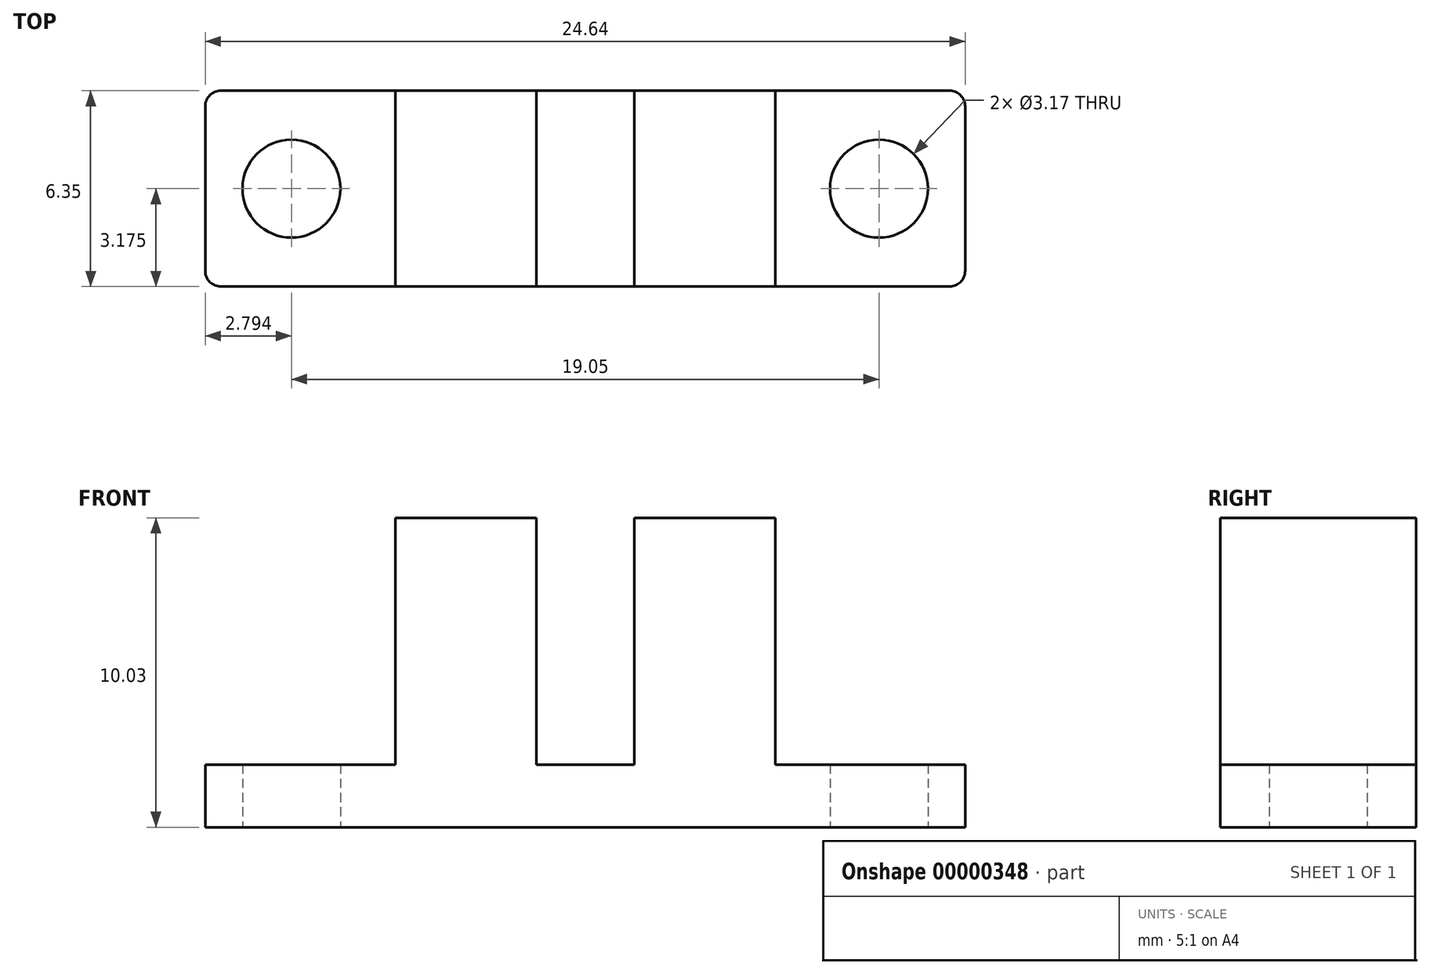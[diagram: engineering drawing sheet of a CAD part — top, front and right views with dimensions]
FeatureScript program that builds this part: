
annotation { "Feature Type Name" : "Feature", "Feature Type Description" : "" }
export const myFeature = defineFeature(function(context is Context, id is Id, definition is map)
    precondition{}
    {
        {
            var Q0;
            Q0=qCreatedBy(makeId("Top.planeOp"),FACE);
            var sketch = newSketch(context, id + "F0", { "sketchPlane" : qUnion([Q0])});
            skLineSegment(sketch, "E0.bottom", {"start": v(0.5, 0) * mm, "end": v(24.13, 0) * mm});
            skLineSegment(sketch, "E0.top", {"start": v(0.5, 6.35) * mm, "end": v(24.13, 6.35) * mm});
            skLineSegment(sketch, "E0.left", {"start": v(0, 0.5) * mm, "end": v(0, 5.84) * mm});
            skLineSegment(sketch, "E0.right", {"start": v(24.64, 0.5) * mm, "end": v(24.64, 5.84) * mm});
            skPoint(sketch, "E1.visualSharp", {"position": v(0, 6.35) * mm});
            skArc(sketch, "E1.filletArc", {"start": v(0.5, 6.35) * mm, "mid": v(0.15, 6.2) * mm, "end": v(0, 5.84) * mm});
            skPoint(sketch, "E2.visualSharp", {"position": v(0, 0) * mm});
            skArc(sketch, "E2.filletArc", {"start": v(0, 0.5) * mm, "mid": v(0.15, 0.15) * mm, "end": v(0.5, 0) * mm});
            skPoint(sketch, "E3.visualSharp", {"position": v(24.64, 0) * mm});
            skArc(sketch, "E3.filletArc", {"start": v(24.13, 0) * mm, "mid": v(24.49, 0.15) * mm, "end": v(24.64, 0.5) * mm});
            skPoint(sketch, "E4.visualSharp", {"position": v(24.64, 6.35) * mm});
            skArc(sketch, "E4.filletArc", {"start": v(24.64, 5.84) * mm, "mid": v(24.49, 6.2) * mm, "end": v(24.13, 6.35) * mm});
            skCircle(sketch, "E5", {"center": v(2.8, 3.18) * mm, "radius": 1.59 * mm});
            skCircle(sketch, "E6", {"center": v(21.84, 3.18) * mm, "radius": 1.59 * mm});
            skSolve(sketch);
        }
        {
            var Q0;
            Q0 = qSketchRegion(id + "F0", true);
            extrude(context, id + "F1", {"entities" : qUnion([Q0]), "depth" : 2.03 * mm});
        }
        {
            var Q0;
            Q0=makeQuery(id+"F1.opExtrude","CAP_FACE",FACE,{"disambiguationData":[OSD([sQuery(id+"F0.wireOp",EDGE,"E0.bottom"),sQuery(id+"F0.wireOp",EDGE,"E0.top"),sQuery(id+"F0.wireOp",EDGE,"E0.left"),sQuery(id+"F0.wireOp",EDGE,"E0.right"),sQuery(id+"F0.wireOp",EDGE,"E1.filletArc"),sQuery(id+"F0.wireOp",EDGE,"E2.filletArc"),sQuery(id+"F0.wireOp",EDGE,"E3.filletArc"),sQuery(id+"F0.wireOp",EDGE,"E4.filletArc"),sQuery(id+"F0.wireOp",EDGE,"E5"),sQuery(id+"F0.wireOp",EDGE,"E6")])],"isStart":false});
            var sketch = newSketch(context, id + "F2", { "sketchPlane" : qUnion([Q0])});
            skLineSegment(sketch, "E7.bottom", {"start": v(6.16, 6.35) * mm, "end": v(10.73, 6.35) * mm});
            skLineSegment(sketch, "E7.top", {"start": v(6.16, 0) * mm, "end": v(10.73, 0) * mm});
            skLineSegment(sketch, "E7.left", {"start": v(6.16, 6.35) * mm, "end": v(6.16, 0) * mm});
            skLineSegment(sketch, "E7.right", {"start": v(10.73, 6.35) * mm, "end": v(10.73, 0) * mm});
            skLineSegment(sketch, "E8.bottom", {"start": v(13.9, 6.35) * mm, "end": v(18.48, 6.35) * mm});
            skLineSegment(sketch, "E8.top", {"start": v(13.9, 0) * mm, "end": v(18.48, 0) * mm});
            skLineSegment(sketch, "E8.left", {"start": v(13.9, 6.35) * mm, "end": v(13.9, 0) * mm});
            skLineSegment(sketch, "E8.right", {"start": v(18.48, 6.35) * mm, "end": v(18.48, 0) * mm});
            skSolve(sketch);
        }
        {
            var Q0;
            Q0 = qSketchRegion(id + "F2", true);
            extrude(context, id + "F3", {"entities" : qUnion([Q0]), "operationType" : NewBodyOperationType.ADD, "depth" : 8 * mm});
        }
    });
